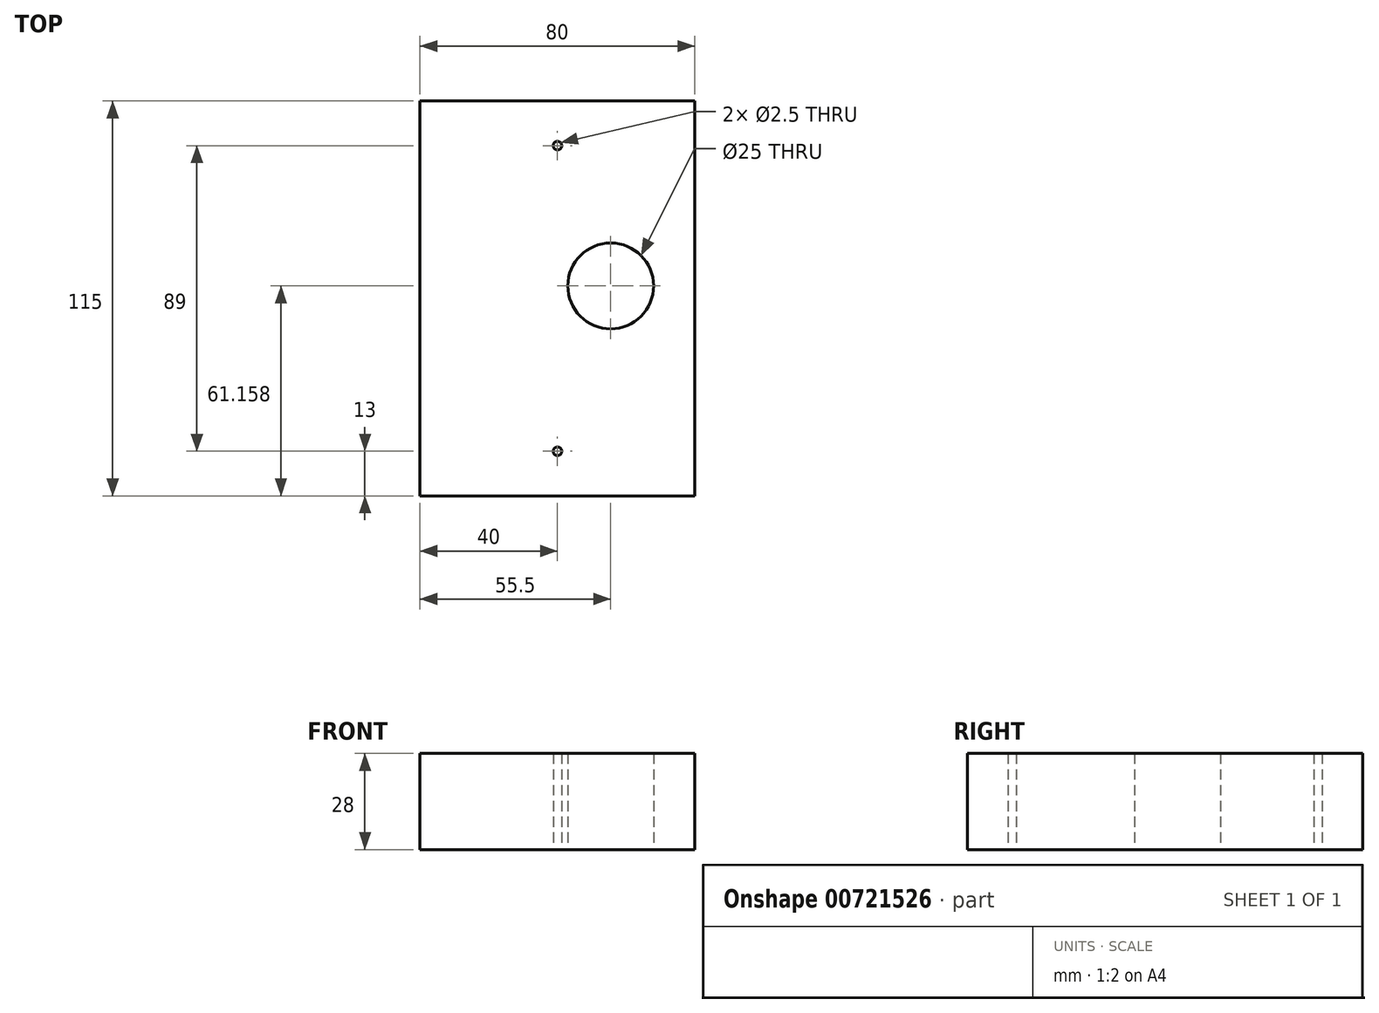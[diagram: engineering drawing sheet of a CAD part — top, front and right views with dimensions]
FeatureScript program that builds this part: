
annotation { "Feature Type Name" : "Feature", "Feature Type Description" : "" }
export const myFeature = defineFeature(function(context is Context, id is Id, definition is map)
    precondition{}
    {
        {
            var Q0;
            Q0=qCreatedBy(makeId("Top.planeOp"),FACE);
            var sketch = newSketch(context, id + "F0", { "sketchPlane" : qUnion([Q0])});
            skLineSegment(sketch, "E0.bottom", {"start": v(0, 115) * mm, "end": v(80, 115) * mm});
            skLineSegment(sketch, "E0.top", {"start": v(0, 0) * mm, "end": v(80, 0) * mm});
            skLineSegment(sketch, "E0.left", {"start": v(0, 115) * mm, "end": v(0, 0) * mm});
            skLineSegment(sketch, "E0.right", {"start": v(80, 115) * mm, "end": v(80, 0) * mm});
            skCircle(sketch, "E1", {"center": v(55.5, 61.16) * mm, "radius": 12.5 * mm});
            skPoint(sketch, "E2", {"position": v(40, 102) * mm});
            skPoint(sketch, "E3", {"position": v(40, 13) * mm});
            skSolve(sketch);
        }
        {
            var Q0;
            Q0=makeQuery(id+"F0.imprint","IMPRINT",FACE,{"disambiguationData":[TD([[makeQuery(id+"F0.imprint","IMPRINT",EDGE,{"derivedFrom":sQuery(id+"F0.wireOp",EDGE,"E0.bottom")}),-1.0]])]});
            extrude(context, id + "F1", {"entities" : qUnion([Q0]), "depth" : 28 * mm, "offsetDistance" : 25 * mm});
        }
        {
            var Q0;
            Q0=sQuery(id+"F0.wireOp",VERTEX,"E3");
            var Q1;
            Q1=sQuery(id+"F0.wireOp",VERTEX,"E2");
            var Q2;
            Q2=makeQuery(id+"F1.opExtrude","SWEPT_BODY",BODY,{"disambiguationData":[OSD([sQuery(id+"F0.wireOp",EDGE,"E0.bottom"),sQuery(id+"F0.wireOp",EDGE,"E0.top"),sQuery(id+"F0.wireOp",EDGE,"E0.left"),sQuery(id+"F0.wireOp",EDGE,"E0.right"),sQuery(id+"F0.wireOp",EDGE,"E1")])]});
            hole(context, id + "F2", {"style" : HoleStyle.SIMPLE, "endStyle" : HoleEndStyle.THROUGH, "oppositeDirection" : true, "standardTappedOrClearance" : lookupTablePath({ "standard" : "ISO", "engagement" : "75%", "pitch" : "0.5 mm", "size" : "M3", "type" : "Tapped" }), "standardBlindInLast" : lookupTablePath({ "standard" : "ISO", "engagement" : "75%", "pitch" : "0.5 mm", "size" : "M3", "type" : "Tapped" }), "holeDiameter" : 2.5 * mm, "majorDiameter" : 3 * mm, "showTappedDepth" : true, "isTappedThrough" : true, "tappedDepth" : 12 * mm, "tapClearance" : 3, "locations" : qUnion([Q0, Q1]), "scope" : qUnion([Q2])});
        }
    });
